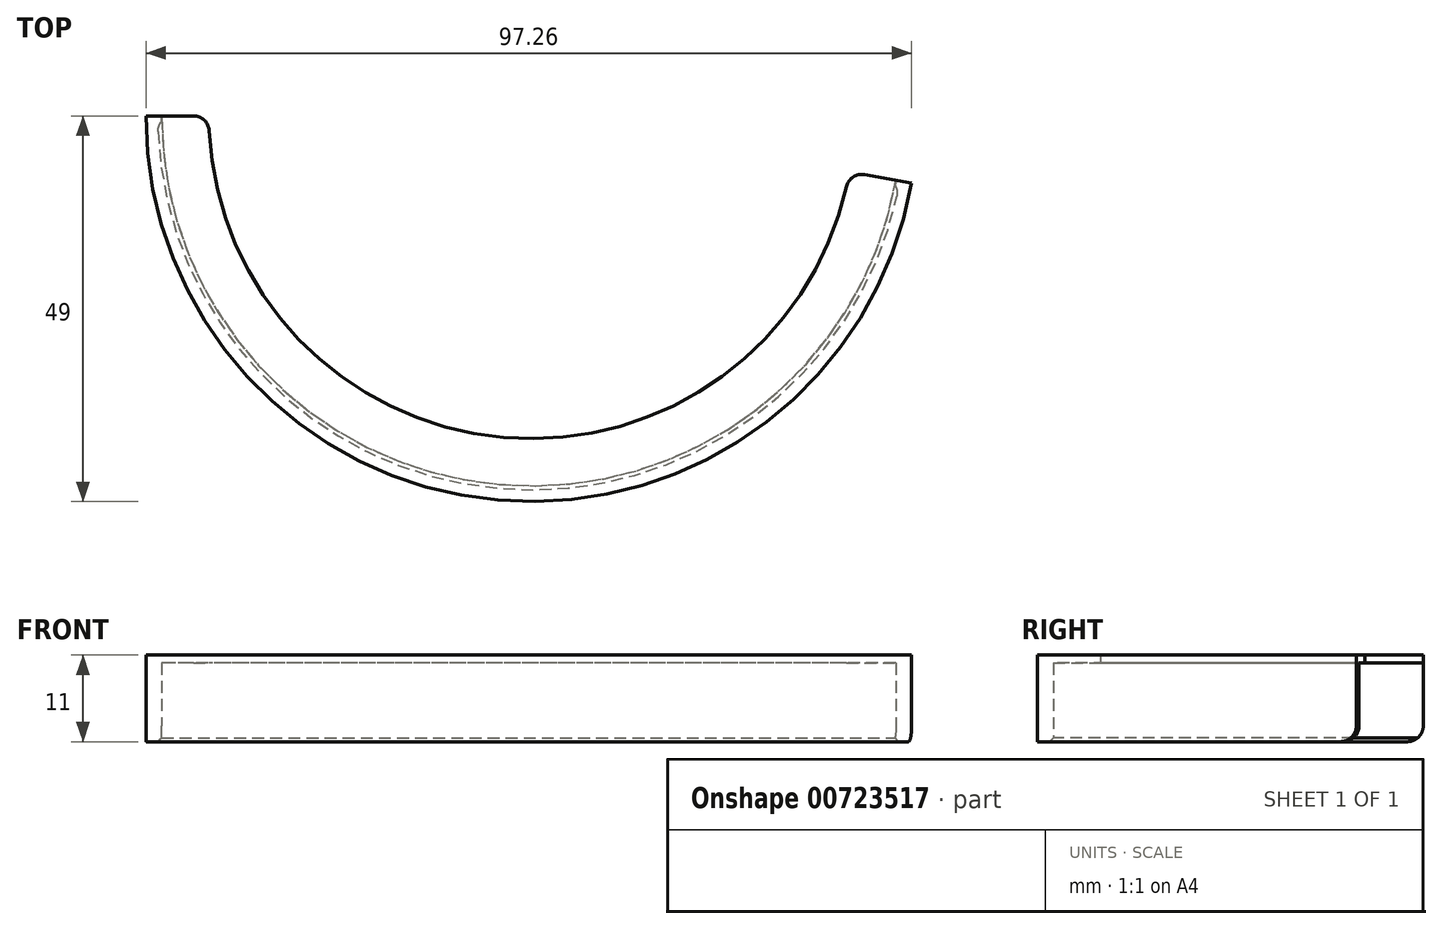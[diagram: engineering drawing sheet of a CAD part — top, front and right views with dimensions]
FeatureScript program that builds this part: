
annotation { "Feature Type Name" : "Feature", "Feature Type Description" : "" }
export const myFeature = defineFeature(function(context is Context, id is Id, definition is map)
    precondition{}
    {
        {
            var Q0;
            Q0=qCreatedBy(makeId("Front.planeOp"),FACE);
            var sketch = newSketch(context, id + "F0", { "sketchPlane" : qUnion([Q0])});
            skLineSegment(sketch, "E0", {"start": v(-49, 0) * mm, "end": v(-49, 11) * mm});
            skLineSegment(sketch, "E1", {"start": v(-49, 11) * mm, "end": v(-41, 11) * mm});
            skLineSegment(sketch, "E2", {"start": v(-41, 10) * mm, "end": v(-41, 11) * mm});
            skLineSegment(sketch, "E3", {"start": v(-41, 10) * mm, "end": v(-47, 10) * mm});
            skLineSegment(sketch, "E4", {"start": v(-47, 10) * mm, "end": v(-47, 0) * mm});
            skLineSegment(sketch, "E5", {"start": v(-49, 0) * mm, "end": v(-47, 0) * mm});
            skLineSegment(sketch, "E6", {"start": v(0, 0) * mm, "end": v(0, 8.5) * mm, "construction": true});
            skSolve(sketch);
        }
        {
            var Q0;
            Q0=makeQuery(id+"F0.imprint","IMPRINT",FACE,{"disambiguationData":[TD([[makeQuery(id+"F0.imprint","IMPRINT",EDGE,{"derivedFrom":sQuery(id+"F0.wireOp",EDGE,"E0")}),-1.0]])]});
            var Q1;
            Q1=sQuery(id+"F0.wireOp",EDGE,"E6");
            revolve(context, id + "F1", {"surfaceOperationType" : NewSurfaceOperationType.NEW, "entities" : qUnion([Q0]), "axis" : qUnion([Q1]), "revolveType" : RevolveType.ONE_DIRECTION, "angle" : 170 * degree});
        }
        {
            var Q0;
            Q0=makeQuery(id+"F1.opRevolve","SWEPT_EDGE",EDGE,{"disambiguationData":[OSD([sQuery(id+"F0.wireOp",EDGE,"E4"),sQuery(id+"F0.wireOp",EDGE,"E5")])]});
            chamfer(context, id + "F2", {"entities" : qUnion([Q0]), "width" : 0.5 * mm, "tangentPropagation" : true});
        }
        {
            var Q0;
            Q0=makeQuery(id+"F1.opRevolve","CAP_EDGE",EDGE,{"disambiguationData":[OSD([sQuery(id+"F0.wireOp",EDGE,"E5")])],"isStart":false});
            var Q1;
            Q1=makeQuery(id+"F1.opRevolve","CAP_EDGE",EDGE,{"disambiguationData":[OSD([sQuery(id+"F0.wireOp",EDGE,"E5")])],"isStart":true});
            var Q2;
            Q2=makeQuery(id+"F1.opRevolve","CAP_EDGE",EDGE,{"disambiguationData":[OSD([sQuery(id+"F0.wireOp",EDGE,"E2")])],"isStart":true});
            var Q3;
            Q3=makeQuery(id+"F1.opRevolve","CAP_EDGE",EDGE,{"disambiguationData":[OSD([sQuery(id+"F0.wireOp",EDGE,"E2")])],"isStart":false});
            fillet(context, id + "F3", {"entities" : qUnion([Q0, Q1, Q2, Q3]), "radius" : 2 * mm, "tangentPropagation" : true, "allowEdgeOverflow" : false});
        }
    });
